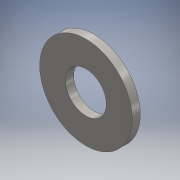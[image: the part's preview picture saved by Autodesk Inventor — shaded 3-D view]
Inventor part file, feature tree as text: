
AUTODESK INVENTOR PART (.ipt)
format: ipt  version: 2016 (Build 200138000, 138)  size: 113,152 bytes
history: native  units: mm
features: extrude x1, sketch x1
ambient origin geometry x8: Origin, YZ Plane, XZ Plane, XY Plane, X Axis, Y Axis, Z Axis, Center Point
bodies: Solid1 (feature_tree)
feature tree (2):
  extrude  "Extrusion1"  Depth=0.6mm
  sketch  "Sketch1"  dims[d0=3.0mm d1=6.8mm d2=0.6mm d3=0.0mm]
